# Revit family: GS55
name_source: partatom
category: Generic Models
units: mm (PartAtom-declared; Revit-internal decimal feet)

## family parameters
Always vertical = Yes
Can host rebar = No
Cut with Voids When Loaded = No
Part Type = Normal
Room Calculation Point = No
Round Connector Dimension = Use Diameter
Shared = Yes
Work Plane-Based = No

## types (2) — shared parameters
Model = GS55°
Type Comments = Neiging 55° tot 65°
URL = https://www.gortergroup.com
lengte trapboom-01 = 3800 mm  [stored 12.4672 ft]
lengte trapboom-02 = 3800 mm  [stored 12.4672 ft]
vaste trap = gietaluminium

## per-type parameters (varying)
| type | afstand trapboom01 | hoogte montagebeugel | hoogte onderste_bovenste treden | trapschuinte |
| GS55_55gr | 160 mm  [stored 0.524934 ft] | 2857 mm  [stored 9.37336 ft] | 3038 mm  [stored 9.96719 ft] | 55.00° |
| GS55_65gr | 154 mm  [stored 0.505249 ft] | 3189 mm  [stored 10.4626 ft] | 3370 mm  [stored 11.0564 ft] | 65.00° |

note: [stored X ft] marks values corroborated as IEEE doubles in the binary element streams (Revit-internal decimal feet)

## geometry (parser evidence)
native form markers: Sweep x8
no freeform markers — native parametric forms only
